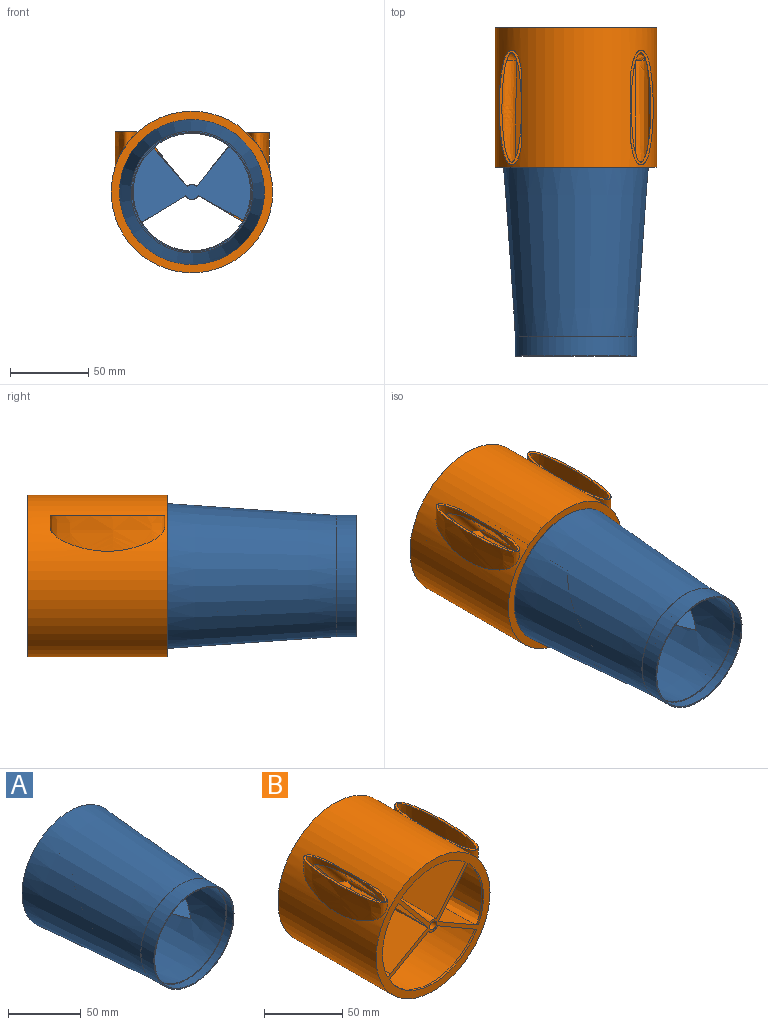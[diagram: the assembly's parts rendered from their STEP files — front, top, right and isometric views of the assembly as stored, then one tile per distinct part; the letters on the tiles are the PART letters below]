
ASSEMBLY  parts=2 mates=1
PART A: 29 faces, bbox 92.5x127x92.5 mm
  f0: cone r=51.59mm half-angle=4deg, axis (0,1,0), area 28890.8mm2, adj f10,f16
  f1: plane 76.2x76.2mm, normal (0,-1,0), area 147.5mm2, adj f8,f13
  f2: plane 82.26x53.03mm, normal (0,-0.71,0.71), area 3463.3mm2, adj f3,f4,f5,f6,f7,f8,f9
  f3: plane 83.32x35.26mm, normal (-0.5,0,-0.87), area 2845mm2, adj f2,f4,f8,f10
  f4: cylinder r=4.76mm len=68.27mm, axis (0,1,0), area 672.7mm2, adj f2,f3,f5,f10
  f5: plane 83.32x35.26mm, normal (0.5,0,-0.87), area 2845mm2, adj f2,f4,f8,f10
  f6: cylinder r=4.76mm len=59.85mm, axis (0,1,0), area 393.1mm2, adj f2,f7,f9,f10
  f7: plane 59.85x31.19mm, normal (-0.77,0,0.64), area 1771.4mm2, adj f2,f6,f8,f10
  f8: cone r=50.8mm half-angle=4deg, axis (0,1,0), area 23010.9mm2, adj f1,f2,f3,f5,f7,f9,f10
  f9: plane 59.85x31.19mm, normal (0.77,0,0.64), area 1771.4mm2, adj f2,f6,f8,f10
  f10: plane 92.53x92.53mm, normal (0,1,0), area 3123.7mm2, adj f0,f3,f4,f5,f6,f7,f8,f9
  f11: cylinder r=3.17mm len=6.35mm, axis (0,1,0), area 126.7mm2, adj f10,f12
  f12: plane 6.35x6.35mm, normal (0,1,0), area 31.7mm2, adj f11
  f13: cylinder r=38.1mm len=76.2mm, axis (0,1,0), area 1520.1mm2, adj f1,f15
  f14: cylinder r=38.89mm len=77.79mm, axis (0,1,0), area 3103.6mm2, adj f15,f16
  f15: plane 77.79x77.79mm, normal (0,-1,0), area 192mm2, adj f13,f14
  f16: plane 77.79x77.79mm, normal (0,1,0), area 43.2mm2, adj f0,f14
  f17: cone r=50.01mm half-angle=4deg, axis (0,1,0), area 2971.2mm2, adj f19,f22,f25,f26
  f18: cone r=50.01mm half-angle=4deg, axis (0,1,0), area 2971.2mm2, adj f19,f20,f24,f26
  f19: plane 80.98x49.76mm, normal (0,0.71,-0.71), area 2987.1mm2, adj f17,f18,f20,f21,f22,f23,f24,f25
  f20: plane 77.85x36.2mm, normal (0.5,0,0.87), area 2710.3mm2, adj f18,f19,f21,f26
  f21: cylinder r=3.17mm len=62.85mm, axis (0,1,0), area 615.3mm2, adj f19,f20,f22,f26
  f22: plane 77.85x36.2mm, normal (-0.5,0,0.87), area 2710.3mm2, adj f17,f19,f21,f26
  f23: cylinder r=3.17mm len=58.58mm, axis (0,1,0), area 444mm2, adj f19,f24,f25,f26
  f24: plane 58.58x32.01mm, normal (0.77,0,-0.64), area 1753mm2, adj f18,f19,f23,f26
  f25: plane 58.58x32.01mm, normal (-0.77,0,-0.64), area 1753mm2, adj f17,f19,f23,f26
  f26: plane 89.13x53.99mm, normal (0,-1,0), area 2518.8mm2, adj f17,f18,f20,f21,f22,f23,f24,f25
  f27: cylinder r=1.59mm len=6.35mm, axis (0,1,0), area 63.3mm2, adj f26,f28
  f28: plane 3.18x3.18mm, normal (0,-1,0), area 7.9mm2, adj f27
PART B: 46 faces, bbox 108.7x293.1x103.6 mm
  f0: plane 101.6x64.32mm, normal (0,1,0), area 3611.2mm2, adj f4,f6,f7,f8,f9,f10,f11,f12
  f1: cylinder r=51.59mm len=103.19mm, axis (0,1,0), area 25596.2mm2, adj f5,f31,f32,f33,f34,f45
  f2: cylinder r=50.01mm len=66.68mm, axis (0,1,0), area 2564.7mm2, adj f15,f23,f29,f40,f42,f44
  f3: cylinder r=50.01mm len=66.68mm, axis (0,1,0), area 2565.7mm2, adj f18,f21,f30,f35,f36,f39
  f4: cylinder r=50.8mm len=101.6mm, axis (0,1,0), area 17284.4mm2, adj f0,f7,f8,f11,f12,f25,f28,f45
  f5: plane 103.32x103.32mm, normal (0,-1,0), area 2318mm2, adj f1,f6,f7,f8,f9,f10,f11,f12
  f6: cylinder r=3.17mm len=76.2mm, axis (0,1,0), area 1520.1mm2, adj f0,f5
  f7: plane 76.2x35.27mm, normal (-0.77,0,0.64), area 3500mm2, adj f0,f4,f5,f9,f27,f28
  f8: plane 76.2x35.27mm, normal (0.77,0,0.64), area 3500mm2, adj f0,f4,f5,f9,f27,f28
  f9: cylinder r=4.76mm len=76.2mm, axis (0,1,0), area 506.7mm2, adj f0,f5,f7,f8
  f10: cylinder r=4.76mm len=76.2mm, axis (0,1,0), area 760.1mm2, adj f0,f5,f11,f12
  f11: plane 76.2x39.87mm, normal (0.5,0,-0.87), area 3500mm2, adj f0,f4,f5,f10,f25,f26
  f12: plane 76.2x39.87mm, normal (-0.5,0,-0.87), area 3500mm2, adj f0,f4,f5,f10,f25,f26
  f13: plane 42.13x31.28mm, normal (0,-1,0), area 707.1mm2, adj f40,f41,f42
  f14: cylinder r=4.76mm len=72.16mm, axis (0,1,0), area 130mm2, adj f5,f15,f16,f40,f41
  f15: plane 68.17x36.18mm, normal (0.77,0.02,-0.64), area 3115.8mm2, adj f2,f5,f14,f23,f24,f40
  f16: plane 68.2x33.74mm, normal (0.5,0.02,0.87), area 2634.2mm2, adj f5,f14,f41,f44
  f17: plane 68.2x33.74mm, normal (-0.5,0.02,0.87), area 2634.2mm2, adj f5,f20,f37,f39
  f18: plane 68.17x36.18mm, normal (-0.77,0.02,-0.64), area 3115.8mm2, adj f3,f5,f20,f21,f22,f35
  f19: plane 42.13x31.28mm, normal (0,-1,0), area 707.1mm2, adj f35,f36,f37
  f20: cylinder r=4.76mm len=72.16mm, axis (0,1,0), area 130mm2, adj f5,f17,f18,f35,f37
  f21: plane 56.52x18.92mm, normal (0,1,0), area 249.9mm2, adj f3,f18,f22,f39
  f22: cylinder r=45.72mm len=52.77mm, axis (0,1,0), area 91mm2, adj f5,f18,f21,f39
  f23: plane 56.52x18.92mm, normal (0,1,0), area 249.9mm2, adj f2,f15,f24,f44
  f24: cylinder r=45.72mm len=52.77mm, axis (0,1,0), area 91mm2, adj f5,f15,f23,f44
  f25: plane 87.99x27.94mm, normal (0,1,0), area 513.5mm2, adj f4,f11,f12,f26
  f26: cylinder r=45.72mm len=79.19mm, axis (0,1,0), area 152mm2, adj f5,f11,f12,f25
  f27: cylinder r=45.72mm len=58.78mm, axis (0,1,0), area 101.3mm2, adj f5,f7,f8,f28
  f28: plane 65.31x15.78mm, normal (0,1,0), area 342.3mm2, adj f4,f7,f8,f27
  f29: extruded ~69.85x22.85mm, area 1707.3mm2, adj f2,f31,f42
  f30: extruded ~69.85x22.85mm, area 1706.2mm2, adj f3,f33,f36
  f31: plane 73.03x14.43mm, normal (0,0,1), area 195mm2, adj f1,f29,f32
  f32: extruded ~72.92x14.42mm, area 0mm2, adj f1,f31
  f33: plane 73.03x14.43mm, normal (0,0,1), area 195mm2, adj f1,f30,f34
  f34: extruded ~72.92x14.42mm, area 0mm2, adj f1,f33
  f35: cylinder r=6.35mm len=39.57mm, axis (0.64,0,-0.77), area 423.9mm2, adj f3,f18,f19,f20,f36,f37
  f36: torus R=43.66mm, axis (0,-1,0), area 493.3mm2, adj f3,f19,f30,f35,f38
  f37: cylinder r=6.35mm len=37.17mm, axis (0.87,0,0.5), area 376.9mm2, adj f17,f19,f20,f35,f38
  f38: sphere r=6.35mm, area 74.7mm2, adj f36,f37,f39
  f39: bspline ~292.67x12.73mm, area 753.1mm2, adj f3,f5,f17,f21,f22,f38
  f40: cylinder r=6.35mm len=39.57mm, axis (-0.64,0,-0.77), area 423.9mm2, adj f2,f13,f14,f15,f41,f42
  f41: cylinder r=6.35mm len=37.17mm, axis (-0.87,0,0.5), area 376.9mm2, adj f13,f14,f16,f40,f43
  f42: torus R=43.66mm, axis (0,-1,0), area 493.3mm2, adj f2,f13,f29,f40,f43
  f43: sphere r=6.35mm, area 69.6mm2, adj f41,f42,f44
  f44: bspline ~292.67x12.73mm, area 753.1mm2, adj f2,f5,f16,f23,f24,f43
  f45: plane 103.19x103.19mm, normal (0,1,0), area 255.3mm2, adj f1,f4
PLACE A rot(axis=(0,-1,0),1.1deg) t=(-35.68,-145.32,-22.7)mm
PLACE B rot(axis=(0,1,0),0.4deg) t=(-35.68,-145.32,-22.7)mm
MATE revolute A.f0 <-> B.f1  axis (0,1,0) through (-35.68,-221.52,-22.7)mm
